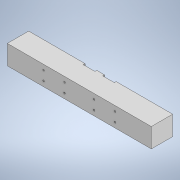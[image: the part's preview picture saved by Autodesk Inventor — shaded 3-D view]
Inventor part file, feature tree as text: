
AUTODESK INVENTOR PART (.ipt)
format: ipt  version: 2020 (Build 240168000, 168)  size: 194,560 bytes
history: native  units: mm
features: other x6, hole x3, sketch x2, projected_geometry x2, extrude x1, mirror x1
ambient origin geometry x8: Origin, YZ Plane, XZ Plane, XY Plane, X Axis, Y Axis, Z Axis, Center Point
bodies: Body1 (feature_tree)
feature tree (15):
  other  "솔리드2"
  other  "작업 평면1"
  other  "작업 평면4"
  extrude  "돌출3"  Depth=25.0mm TaperAngle=0.0deg
  hole  "구멍1"  [1 undecoded]
  hole  "구멍2"  [1 undecoded]
  hole  "구멍3"  [1 undecoded]
  mirror  "미러1"
  sketch  "스케치4"
  sketch  "스케치6"
  projected_geometry  "투영된 루프4"
  projected_geometry  "투영된 루프5"
  other  "<userpath>\Documents\Inventor\CoMoVi\Design4\v4.iam"
  other  "v4.iam"
  other  "AL_profile_final:1"
note: 3 required parameter values undecoded (feature->parameter linkage not recoverable at this tier; creation-order binding heuristic only, values carry confidence <= 0.55)
